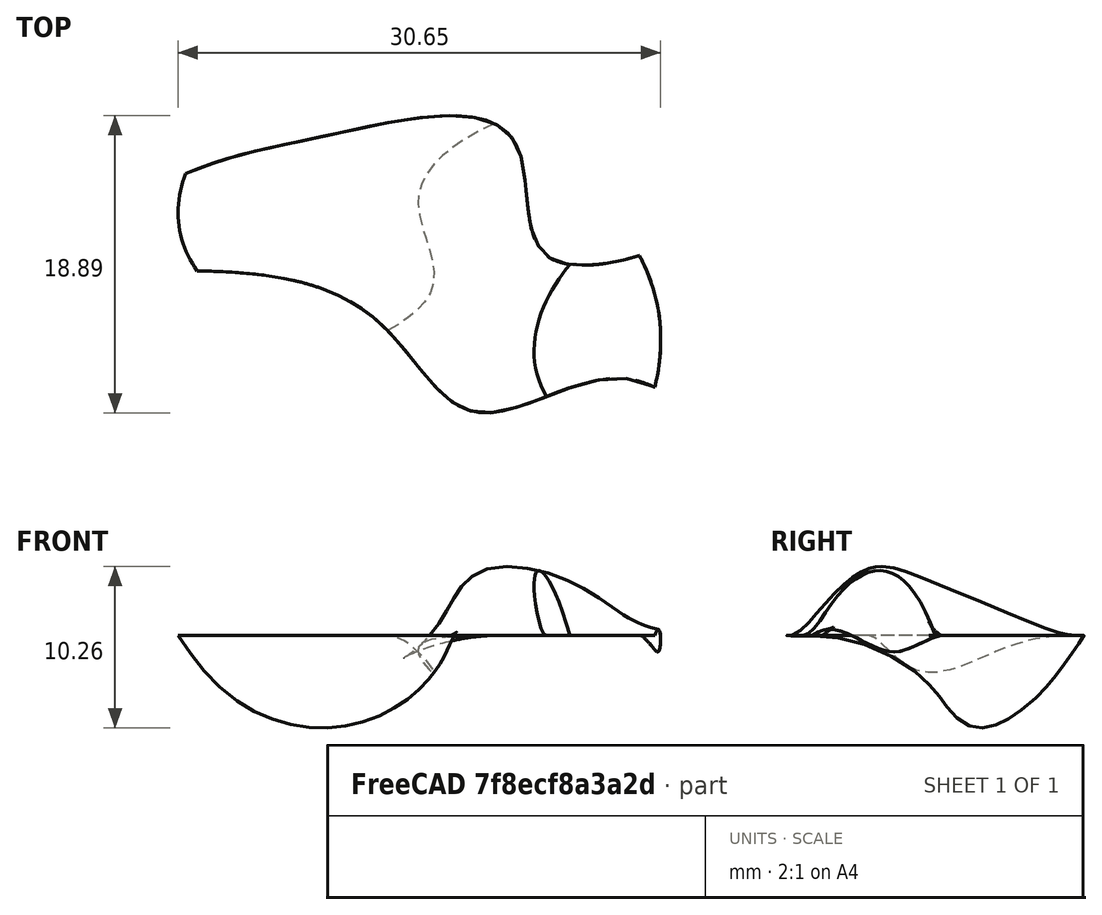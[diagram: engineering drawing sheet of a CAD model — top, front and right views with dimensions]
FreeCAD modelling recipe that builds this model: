
FCSTD DOCUMENT  (FreeCAD 0.18R14859 (Git))
Label: TiGL-tests
License: All rights reserved
LicenseURL: http://en.wikipedia.org/wiki/All_rights_reserved
objects: Part::Feature×19, Part::Compound×9
note: 28 computed .brp shape members not serialized (recipe doc carries the construction recipe); baked Part::Feature solids carry a one-line shape summary decoded from their .brp

FEATURE [Part::Feature] guides
  shape: bbox 29.77 x 3.272 x 3.415 mm, 0 faces, 0 solids (baked)
FEATURE [Part::Feature] profiles
  shape: bbox 29.77 x 3.663 x 3.257 mm, 0 faces, 0 solids (baked)
FEATURE [Part::Compound] Compound  label="Belly_Fairing"
  Links = -> [guides,profiles]
FEATURE [Part::Feature] guides001
  shape: bbox 4371 x 1974 x 2126 mm, 0 faces, 0 solids (baked)
FEATURE [Part::Feature] profiles001
  shape: bbox 4185 x 2017 x 2116 mm, 0 faces, 0 solids (baked)
FEATURE [Part::Compound] Compound001  label="Full_Nacelle"
  Links = -> [guides001,profiles001]
FEATURE [Part::Feature] guides002
  shape: bbox 37.79 x 3.96 x 4.149 mm, 0 faces, 0 solids (baked)
FEATURE [Part::Feature] profiles002
  shape: bbox 37.77 x 3.953 x 4.142 mm, 0 faces, 0 solids (baked)
FEATURE [Part::Compound] Compound002  label="Fuselage"
  Links = -> [guides002,profiles002]
FEATURE [Part::Feature] guides003
  shape: bbox 1.998 x 0.3275 x 0.3826 mm, 0 faces, 0 solids (baked)
FEATURE [Part::Feature] profiles003
  shape: bbox 1.998 x 0.3275 x 0.3827 mm, 0 faces, 0 solids (baked)
FEATURE [Part::Compound] Compound003  label="Heli_Body"
  Links = -> [guides003,profiles003]
FEATURE [Part::Feature] guides004
  shape: bbox 2600 x 580.4 x 1158 mm, 0 faces, 0 solids (baked)
FEATURE [Part::Feature] profiles004
  shape: bbox 2603 x 2e-07 x 1252 mm, 0 faces, 0 solids (baked)
FEATURE [Part::Compound] Compound004  label="Nacelle"
  Links = -> [guides004,profiles004]
FEATURE [Part::Feature] guides005
  shape: bbox 1.164 x 2.414 x 0.9236 mm, 0 faces, 0 solids (baked)
FEATURE [Part::Feature] profiles005
  shape: bbox 1.164 x 2.462 x 1.022 mm, 0 faces, 0 solids (baked)
FEATURE [Part::Compound] Compound005  label="Spiral_Wing"
  Links = -> [guides005,profiles005]
FEATURE [Part::Feature] guides006
  shape: bbox 29.8 x 19.81 x 2e-07 mm, 0 faces, 0 solids (baked)
FEATURE [Part::Feature] profiles006
  shape: bbox 30.88 x 17.34 x 7.32 mm, 0 faces, 0 solids (baked)
FEATURE [Part::Feature] guides007
  shape: bbox 24.21 x 29.61 x 3.734 mm, 0 faces, 0 solids (baked)
FEATURE [Part::Feature] profiles007
  shape: bbox 24.25 x 29.64 x 4.64 mm, 0 faces, 0 solids (baked)
FEATURE [Part::Compound] Compound007  label="Wing_2"
  Links = -> [guides007,profiles007]
FEATURE [Part::Feature] guides008
  shape: bbox 9.393 x 16.96 x 1.257 mm, 0 faces, 0 solids (baked)
FEATURE [Part::Feature] profiles008
  shape: bbox 9.395 x 16.96 x 1.741 mm, 0 faces, 0 solids (baked)
FEATURE [Part::Compound] Compound008  label="Wing_3"
  Links = -> [guides008,profiles008]
FEATURE [Part::Feature] result_gordon
  shape: bbox 30.66 x 19.17 x 10.61 mm, 1 faces, 0 solids (baked)
FEATURE [Part::Compound] Compound006  label="Test_Surface_4"
  Links = -> [guides006,profiles006,result_gordon]
